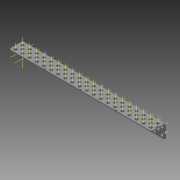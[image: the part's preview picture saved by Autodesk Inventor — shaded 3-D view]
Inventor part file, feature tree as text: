
AUTODESK INVENTOR PART (.ipt)
format: ipt  version: 2015 (Build 190159000, 159)  size: 2,148,864 bytes
history: native  units: in
note: dims shown in document units (in); Inventor stores cm internally (conversion verified against a paired STEP export)
features: other x125, pattern_linear x4, sheet_metal_op x1, extrude x1, imported_body x1, sketch x1
ambient origin geometry x8: Origin, YZ Plane, XZ Plane, XY Plane, X Axis, Y Axis, Z Axis, Center Point
bodies: Body1 (feature_tree)
feature tree (133):
  sheet_metal_op  "Fold1"
  other  "L-Channel"
  extrude  "length cut"  Depth=0.5in
  other  "top out axis"
  other  "top inner axis"
  other  "back out axis"
  other  "back inner axis"
  pattern_linear  "top outer axes"  Count1=2 Spacing1=0.5in
  pattern_linear  "top inner axes"  Spacing1=0.5in  [1 undecoded]
  pattern_linear  "back outer axes"  Count1=2 Spacing1=0.5in
  pattern_linear  "back inner axes"  Spacing1=0.5in  [1 undecoded]
  other  "right plane"
  imported_body  "Base1"
  sketch  "Sketch1"  dims[d1=0.0in d4=0.5in d5=0.7874in d7=0.5in d10=0.5in d13=0.5in d14=0.7874in d16=0.5in d19=0.5in d20=-10.0in d21=0.0in d22=0.0in d23=0.0in d24=0.0in d25=0.0in d26=0.0in]
  other  "Work Point1"
  other  "Work Point2"
  other  "Work Point3"
  other  "Work Point4"
  other  "Work Axis5"
  other  "Work Axis6"
  other  "Work Axis7"
  other  "Work Axis8"
  other  "Work Axis11"
  other  "Work Axis12"
  other  "Work Axis13"
  other  "Work Axis14"
  other  "Work Axis15"
  other  "Work Axis18"
  other  "Work Axis19"
  other  "Work Axis20"
  other  "Work Axis23"
  other  "Work Axis24"
  other  "Work Axis25"
  other  "Work Axis26"
  other  "Work Axis29"
  other  "Work Axis30"
  other  "Work Axis31"
  other  "Work Axis32"
  other  "Work Axis33"
  other  "Work Axis36"
  other  "Work Axis37"
  other  "Work Axis38"
  other  "Work Axis41"
  other  "Work Axis42"
  other  "Work Axis43"
  other  "Work Axis44"
  other  "Work Axis45"
  other  "Work Axis46"
  other  "Work Axis47"
  other  "Work Axis48"
  other  "Work Axis49"
  other  "Work Axis50"
  other  "Work Axis51"
  other  "Work Axis52"
  other  "Work Axis53"
  other  "Work Axis54"
  other  "Work Axis55"
  other  "Work Axis61"
  other  "Work Axis62"
  other  "Work Axis63"
  other  "Work Axis64"
  other  "Work Axis65"
  other  "Work Axis66"
  other  "Work Axis67"
  other  "Work Axis68"
  other  "Work Axis69"
  other  "Work Axis70"
  other  "Work Axis71"
  other  "Work Axis72"
  other  "Work Axis73"
  other  "Work Axis74"
  other  "Work Axis75"
  other  "Work Axis81"
  other  "Work Axis82"
  other  "Work Axis83"
  other  "Work Axis84"
  other  "Work Axis85"
  other  "Work Axis86"
  other  "Work Axis87"
  other  "Work Axis88"
  other  "Work Axis89"
  other  "Work Axis90"
  other  "Work Axis91"
  other  "Work Axis92"
  other  "Work Axis93"
  other  "Work Axis94"
  other  "Work Axis95"
  other  "Work Axis101"
  other  "Work Axis102"
  other  "Work Axis103"
  other  "Work Axis104"
  other  "Work Axis105"
  other  "Work Axis106"
  other  "Work Axis107"
  other  "Work Axis108"
  other  "Work Axis109"
  other  "Work Axis110"
  other  "Work Axis111"
  other  "Work Axis112"
  other  "Work Axis113"
  other  "Work Axis114"
  other  "Work Axis115"
  other  "Work Axis121"
  other  "Work Axis122"
  other  "Work Axis123"
  other  "Work Axis124"
  other  "Work Axis125"
  other  "Work Axis126"
  other  "Work Axis127"
  other  "Work Axis128"
  other  "Work Axis129"
  other  "Work Axis130"
  other  "Work Axis131"
  other  "Work Axis132"
  other  "Work Axis133"
  other  "Work Axis134"
  other  "Work Axis135"
  other  "Work Axis141"
  other  "Work Axis142"
  other  "Work Axis143"
  other  "Work Axis144"
  other  "Work Axis145"
  other  "Work Axis146"
  other  "Work Axis147"
  other  "Work Axis148"
  other  "Work Axis149"
  other  "Work Axis150"
  other  "Work Axis151"
  other  "Work Axis152"
  other  "Work Axis153"
  other  "Work Axis154"
  other  "Work Axis155"
  other  "left plane"
note: 2 required parameter values undecoded (feature->parameter linkage not recoverable at this tier; creation-order binding heuristic only, values carry confidence <= 0.55)
